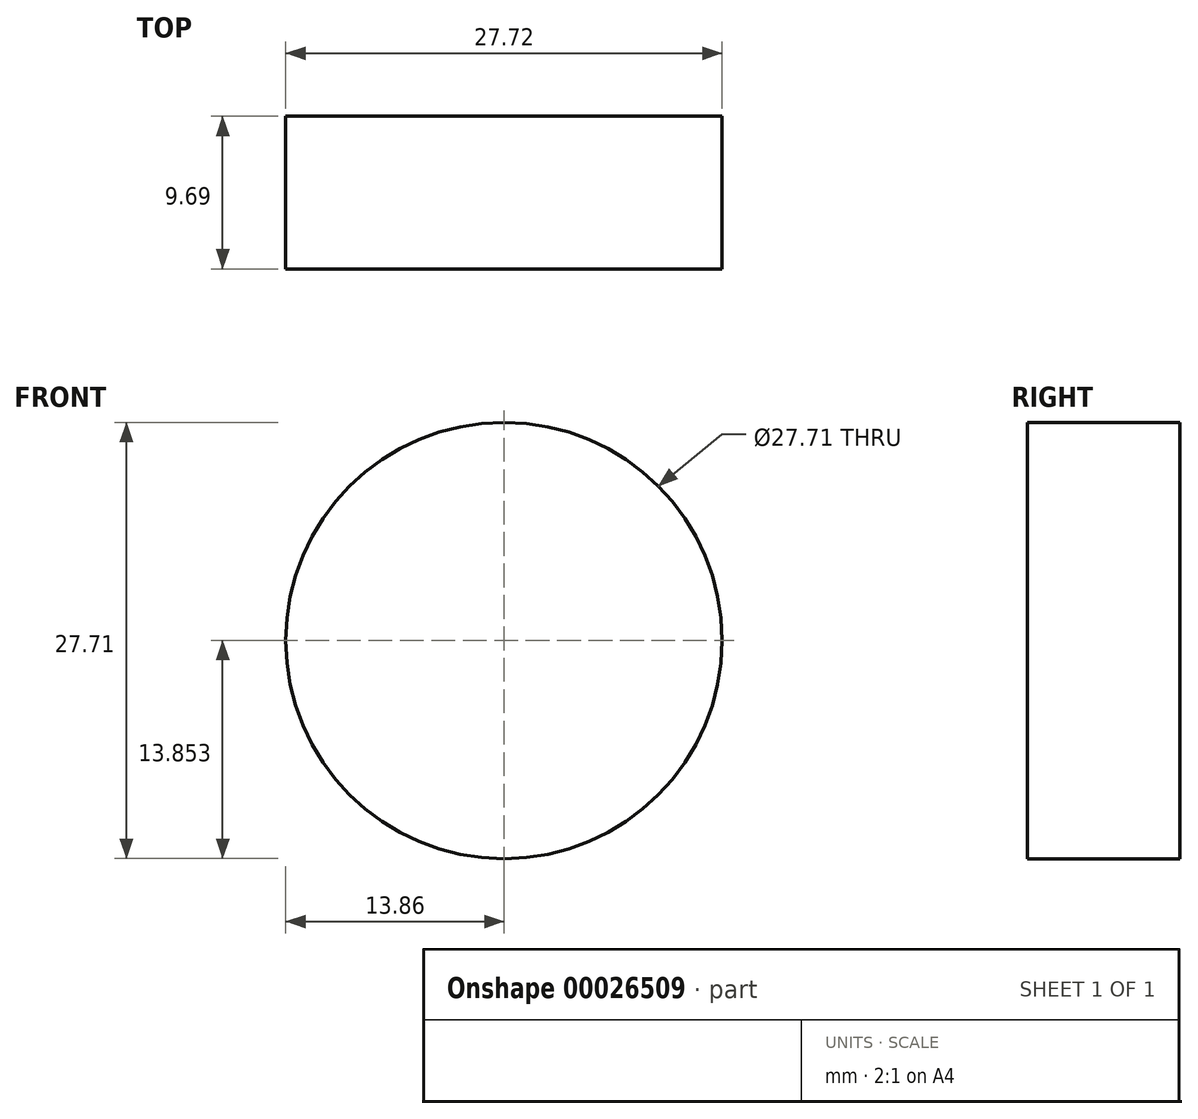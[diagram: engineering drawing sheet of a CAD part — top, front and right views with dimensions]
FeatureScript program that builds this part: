
annotation { "Feature Type Name" : "Feature", "Feature Type Description" : "" }
export const myFeature = defineFeature(function(context is Context, id is Id, definition is map)
    precondition{}
    {
        {
            var Q0;
            Q0=qCreatedBy(makeId("Front.planeOp"),FACE);
            var sketch = newSketch(context, id + "F0", { "sketchPlane" : qUnion([Q0])});
            skCircle(sketch, "E0", {"center": v(-15.67, 9.42) * mm, "radius": 13.86 * mm});
            skSolve(sketch);
        }
        {
            var Q0;
            Q0=sQuery(id+"F0.wireOp",EDGE,"E0");
            extrude(context, id + "F1", {"bodyType" : ToolBodyType.SURFACE, "surfaceEntities" : qUnion([Q0]), "oppositeDirection" : true, "depth" : 9.7 * mm});
        }
    });
